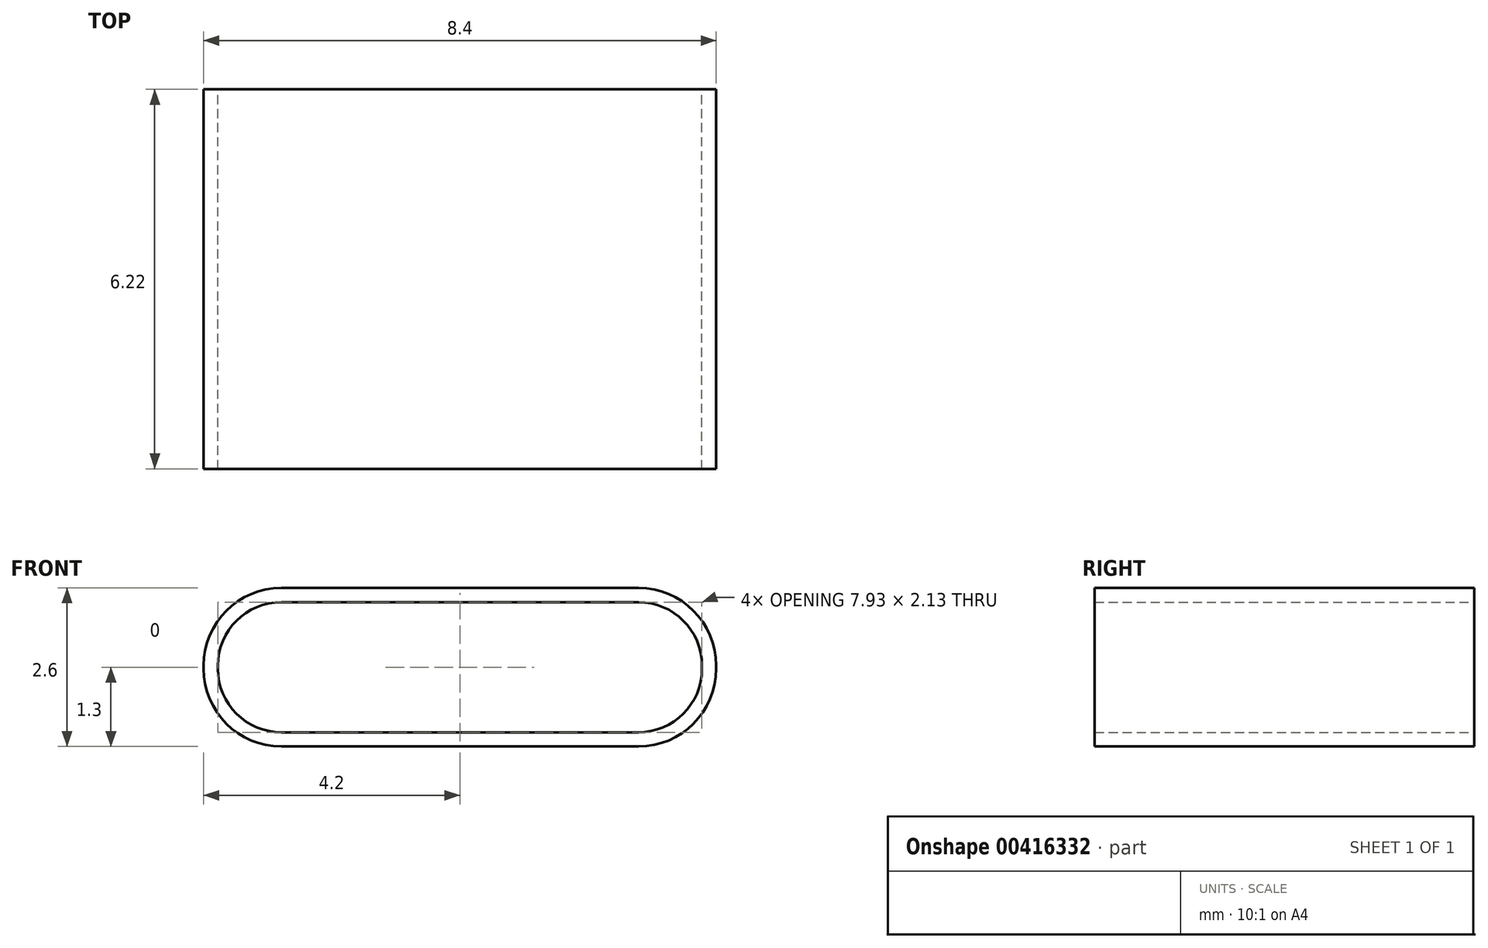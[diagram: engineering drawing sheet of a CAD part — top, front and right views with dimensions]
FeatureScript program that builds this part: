
annotation { "Feature Type Name" : "Feature", "Feature Type Description" : "" }
export const myFeature = defineFeature(function(context is Context, id is Id, definition is map)
    precondition{}
    {
        {
            var Q0;
            Q0=qCreatedBy(makeId("Front.planeOp"),FACE);
            var sketch = newSketch(context, id + "F0", { "sketchPlane" : qUnion([Q0])});
            skLineSegment(sketch, "E0.bottom", {"start": v(2.93, 1.3) * mm, "end": v(-2.93, 1.3) * mm});
            skLineSegment(sketch, "E0.top", {"start": v(2.93, -1.3) * mm, "end": v(-2.93, -1.3) * mm});
            skLineSegment(sketch, "E0.left", {"start": v(4.2, 0.03) * mm, "end": v(4.2, -0.03) * mm});
            skLineSegment(sketch, "E0.right", {"start": v(-4.2, 0.03) * mm, "end": v(-4.2, -0.03) * mm});
            skPoint(sketch, "E0.middle", {"position": v(0, 0) * mm});
            skPoint(sketch, "E1.visualSharp", {"position": v(-4.2, 1.3) * mm});
            skArc(sketch, "E1.filletArc", {"start": v(-2.93, 1.3) * mm, "mid": v(-3.83, 0.93) * mm, "end": v(-4.2, 0.03) * mm});
            skPoint(sketch, "E2.visualSharp", {"position": v(-4.2, -1.3) * mm});
            skArc(sketch, "E2.filletArc", {"start": v(-4.2, -0.03) * mm, "mid": v(-3.83, -0.93) * mm, "end": v(-2.93, -1.3) * mm});
            skPoint(sketch, "E3.visualSharp", {"position": v(4.2, 1.3) * mm});
            skArc(sketch, "E3.filletArc", {"start": v(4.2, 0.03) * mm, "mid": v(3.83, 0.93) * mm, "end": v(2.93, 1.3) * mm});
            skPoint(sketch, "E4.visualSharp", {"position": v(4.2, -1.3) * mm});
            skArc(sketch, "E4.filletArc", {"start": v(2.93, -1.3) * mm, "mid": v(3.83, -0.93) * mm, "end": v(4.2, -0.03) * mm});
            skLineSegment(sketch, "E5.1", {"start": v(4.1, 0.03) * mm, "end": v(4.1, -0.03) * mm});
            skLineSegment(sketch, "E5.5", {"start": v(-4.1, 0.03) * mm, "end": v(-4.1, -0.03) * mm});
            skArc(sketch, "E6.0", {"start": v(3.97, 0.03) * mm, "mid": v(3.66, 0.76) * mm, "end": v(2.93, 1.07) * mm});
            skLineSegment(sketch, "E6.1", {"start": v(3.97, 0.03) * mm, "end": v(3.97, -0.03) * mm});
            skLineSegment(sketch, "E6.2", {"start": v(2.93, 1.07) * mm, "end": v(-2.93, 1.07) * mm});
            skArc(sketch, "E6.3", {"start": v(2.93, -1.07) * mm, "mid": v(3.66, -0.76) * mm, "end": v(3.97, -0.03) * mm});
            skArc(sketch, "E6.4", {"start": v(-2.93, 1.07) * mm, "mid": v(-3.66, 0.76) * mm, "end": v(-3.97, 0.03) * mm});
            skLineSegment(sketch, "E6.5", {"start": v(-3.97, 0.03) * mm, "end": v(-3.97, -0.03) * mm});
            skArc(sketch, "E6.6", {"start": v(-3.97, -0.03) * mm, "mid": v(-3.66, -0.76) * mm, "end": v(-2.93, -1.07) * mm});
            skLineSegment(sketch, "E6.7", {"start": v(2.93, -1.07) * mm, "end": v(-2.93, -1.07) * mm});
            skSolve(sketch);
        }
        {
            var Q0;
            Q0=makeQuery(id+"F0.imprint","IMPRINT",FACE,{"disambiguationData":[TD([[makeQuery(id+"F0.imprint","IMPRINT",EDGE,{"derivedFrom":sQuery(id+"F0.wireOp",EDGE,"E0.bottom")}),1.0]])]});
            extrude(context, id + "F1", {"entities" : qUnion([Q0]), "depth" : 6.22 * mm});
        }
    });
